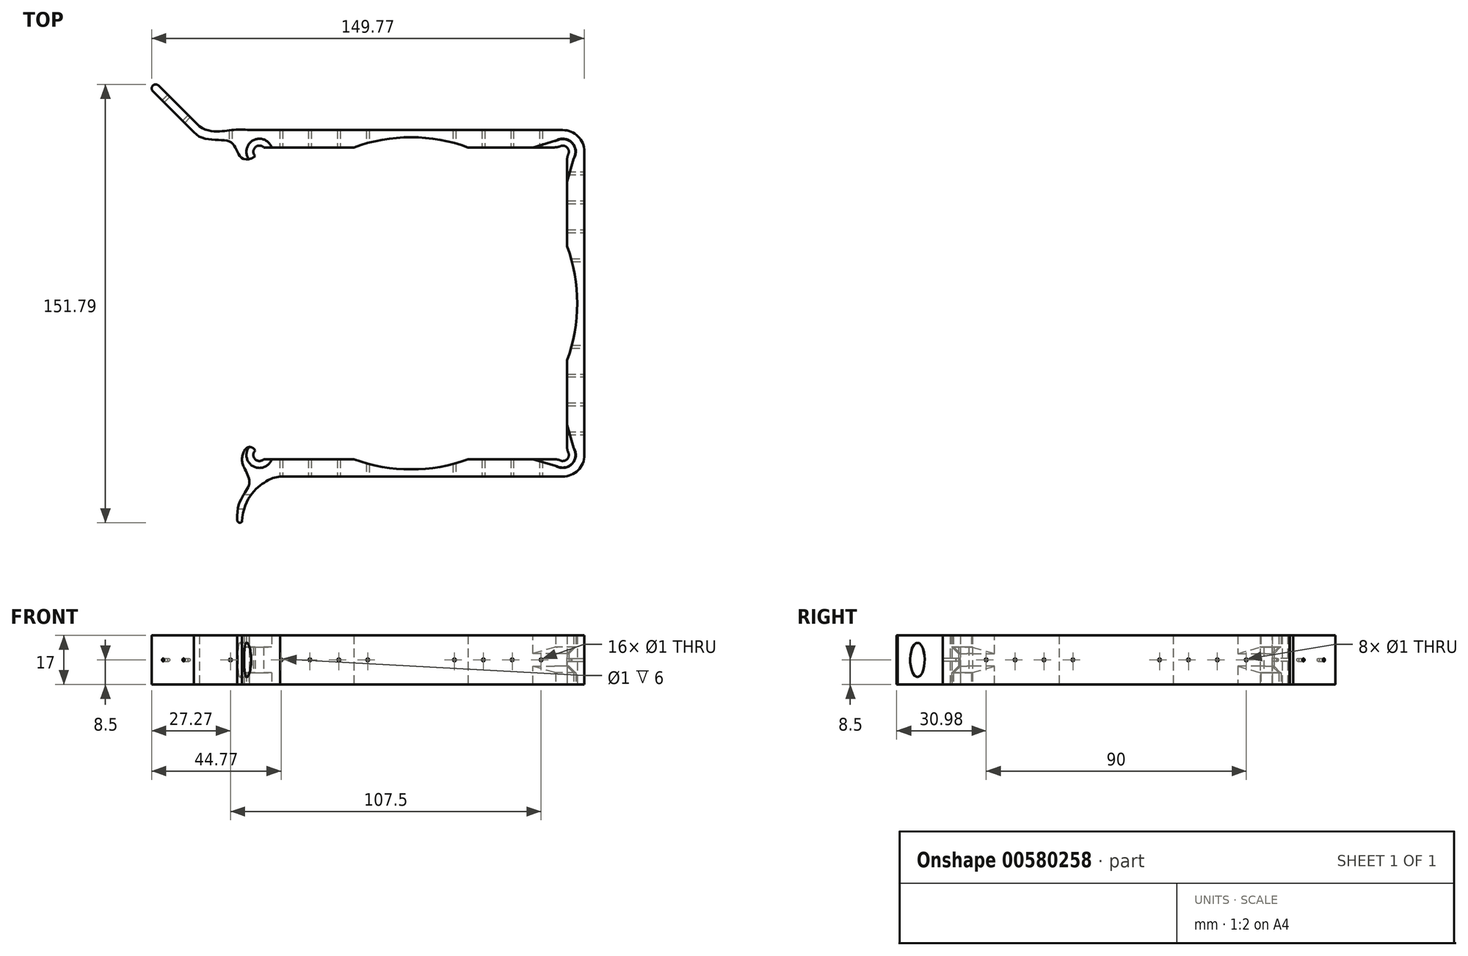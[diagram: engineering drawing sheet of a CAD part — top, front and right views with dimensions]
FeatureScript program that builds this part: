
annotation { "Feature Type Name" : "Feature", "Feature Type Description" : "" }
export const myFeature = defineFeature(function(context is Context, id is Id, definition is map)
    precondition{}
    {
        {
            var Q0;
            Q0=qCreatedBy(makeId("Top.planeOp"),FACE);
            var sketch = newSketch(context, id + "F0", { "sketchPlane" : qUnion([Q0])});
            skLineSegment(sketch, "E0.0", {"start": v(-52.5, 60) * mm, "end": v(52.5, 60) * mm});
            skLineSegment(sketch, "E0.1", {"start": v(60, -52.5) * mm, "end": v(60, 52.5) * mm});
            skArc(sketch, "E0.2", {"start": v(52.5, 60) * mm, "mid": v(57.8, 57.8) * mm, "end": v(60, 52.5) * mm});
            skArc(sketch, "E0.3", {"start": v(60, -52.5) * mm, "mid": v(57.8, -57.8) * mm, "end": v(52.5, -60) * mm});
            skLineSegment(sketch, "E0.4", {"start": v(-52.5, -60) * mm, "end": v(52.5, -60) * mm});
            skCircle(sketch, "E0.6", {"center": v(-52.5, -52.5) * mm, "radius": 2.1 * mm});
            skCircle(sketch, "E0.7", {"center": v(52.5, -52.5) * mm, "radius": 2.1 * mm});
            skCircle(sketch, "E0.8", {"center": v(52.5, 52.5) * mm, "radius": 2.1 * mm});
            skCircle(sketch, "E0.9", {"center": v(-52.5, 52.5) * mm, "radius": 2.1 * mm});
            skLineSegment(sketch, "E1", {"start": v(54, 51.03) * mm, "end": v(54, -51.03) * mm});
            skLineSegment(sketch, "E2", {"start": v(51.03, -54) * mm, "end": v(-51.03, -54) * mm});
            skLineSegment(sketch, "E3", {"start": v(-51.03, 54) * mm, "end": v(51.03, 54) * mm});
            skArc(sketch, "E4", {"start": v(-52.5, -60) * mm, "mid": v(-57.8, -56.8) * mm, "end": v(-57.46, -50.62) * mm});
            skArc(sketch, "E5", {"start": v(-57.46, -50.62) * mm, "mid": v(-55.6, -49.77) * mm, "end": v(-53.98, -51.01) * mm});
            skFitSpline(sketch, "E6", {"points": [v(-52.5, 60) * mm, v(-62.19, 60) * mm, v(-73.29, 61.27) * mm], "startDerivative": vector(-27.31, 0) * mm, "endDerivative": vector(-24.95, 15.44) * mm});
            skFitSpline(sketch, "E7", {"points": [v(-75.23, 59.33) * mm, v(-62.19, 55.68) * mm, v(-57.14, 49.87) * mm], "startDerivative": vector(19.56, -22.5) * mm, "endDerivative": vector(22.3, -1.77) * mm});
            skArc(sketch, "E8", {"start": v(-57.14, 49.87) * mm, "mid": v(-55.44, 50.1) * mm, "end": v(-54, 51.03) * mm});
            skLineSegment(sketch, "E9", {"start": v(-51.03, 54) * mm, "end": v(-54, 51.03) * mm, "construction": true});
            skLineSegment(sketch, "E10", {"start": v(-75.23, 59.33) * mm, "end": v(-73.29, 61.27) * mm, "construction": true});
            skLineSegment(sketch, "E11", {"start": v(-75.23, 59.33) * mm, "end": v(-89.37, 73.47) * mm});
            skLineSegment(sketch, "E12", {"start": v(-73.29, 61.27) * mm, "end": v(-87.43, 75.4) * mm});
            skLineSegment(sketch, "E13", {"start": v(-87.43, 75.4) * mm, "end": v(-89.37, 73.47) * mm});
            skArc(sketch, "E14", {"start": v(-89.37, 73.47) * mm, "mid": v(-89.37, 75.4) * mm, "end": v(-87.43, 75.4) * mm});
            skCircle(sketch, "E15.0", {"center": v(0, 0) * mm, "radius": 57.5 * mm});
            skCircle(sketch, "E16", {"center": v(52.5, 52.5) * mm, "radius": 4.5 * mm});
            skCircle(sketch, "E17", {"center": v(-52.5, 52.5) * mm, "radius": 4.5 * mm});
            skCircle(sketch, "E18", {"center": v(-52.5, -52.5) * mm, "radius": 4.5 * mm});
            skCircle(sketch, "E19", {"center": v(52.5, -52.5) * mm, "radius": 4.5 * mm});
            skFitSpline(sketch, "E20", {"points": [v(-57.8, -56.8) * mm, v(-56.05, -62.69) * mm, v(-60.16, -75.14) * mm], "startDerivative": vector(6.66, -14.28) * mm, "endDerivative": vector(2.44, -37.2) * mm});
            skFitSpline(sketch, "E21", {"points": [v(-45.27, -60) * mm, v(-50.57, -61.9) * mm, v(-58.55, -75.64) * mm], "startDerivative": vector(-16.83, -1.28) * mm, "endDerivative": vector(-1.83, -37.37) * mm});
            skArc(sketch, "E22", {"start": v(-60.16, -75.14) * mm, "mid": v(-59.53, -75.94) * mm, "end": v(-58.55, -75.64) * mm});
            skSolve(sketch);
        }
        {
            var Q0;
            Q0=makeQuery(id+"F0.imprint","IMPRINT",FACE,{"disambiguationData":[TD([[makeQuery(id+"F0.imprint","IMPRINT",EDGE,{"derivedFrom":sQuery(id+"F0.wireOp",EDGE,"E0.0")}),-1.0]])]});
            var Q1;
            Q1=makeQuery(id+"F0.imprint","IMPRINT",FACE,{"disambiguationData":[TD([[makeQuery(id+"F0.imprint","IMPRINT",EDGE,{"derivedFrom":sQuery(id+"F0.wireOp",EDGE,"E13")}),-1.0]])]});
            var Q2;
            {var subQ0=sQuery(id+"F0.wireOp",EDGE,"E3");var subQ1=sQuery(id+"F0.wireOp",EDGE,"E0.9");var subQ2=makeQuery(id+"F0.imprint","INTERSECT",VERTEX,{"derivedFrom":[subQ1,subQ0]});Q2=makeQuery(id+"F0.imprint","IMPRINT",FACE,{"disambiguationData":[TD([[makeQuery(id+"F0.imprint","IMPRINT",EDGE,{"disambiguationData":[TD([[subQ2,-1.0]])],"derivedFrom":subQ1}),-1.0]])]});}
            var Q3;
            {var subQ0=sQuery(id+"F0.wireOp",EDGE,"E1");var subQ1=sQuery(id+"F0.wireOp",EDGE,"E0.8");var subQ2=makeQuery(id+"F0.imprint","INTERSECT",VERTEX,{"derivedFrom":[subQ1,subQ0]});Q3=makeQuery(id+"F0.imprint","IMPRINT",FACE,{"disambiguationData":[TD([[makeQuery(id+"F0.imprint","IMPRINT",EDGE,{"disambiguationData":[TD([[subQ2,-1.0]])],"derivedFrom":subQ1}),-1.0]])]});}
            var Q4;
            {var subQ0=sQuery(id+"F0.wireOp",EDGE,"E1");var subQ1=sQuery(id+"F0.wireOp",EDGE,"E0.7");var subQ2=makeQuery(id+"F0.imprint","INTERSECT",VERTEX,{"derivedFrom":[subQ1,subQ0]});Q4=makeQuery(id+"F0.imprint","IMPRINT",FACE,{"disambiguationData":[TD([[makeQuery(id+"F0.imprint","IMPRINT",EDGE,{"disambiguationData":[TD([[subQ2,1.0]])],"derivedFrom":subQ1}),-1.0]])]});}
            var Q5;
            {var subQ0=sQuery(id+"F0.wireOp",EDGE,"E2");var subQ1=sQuery(id+"F0.wireOp",EDGE,"E0.6");var subQ2=makeQuery(id+"F0.imprint","INTERSECT",VERTEX,{"derivedFrom":[subQ1,subQ0]});Q5=makeQuery(id+"F0.imprint","IMPRINT",FACE,{"disambiguationData":[TD([[makeQuery(id+"F0.imprint","IMPRINT",EDGE,{"disambiguationData":[TD([[subQ2,1.0]])],"derivedFrom":subQ1}),-1.0]])]});}
            extrude(context, id + "F1", {"entities" : qUnion([Q0, Q1, Q2, Q3, Q4, Q5]), "endBound" : BoundingType.SYMMETRIC, "depth" : 9 * mm, "offsetDistance" : 25 * mm});
        }
        {
            var Q0;
            Q0=makeQuery(id+"F0.imprint","IMPRINT",FACE,{"disambiguationData":[TD([[makeQuery(id+"F0.imprint","IMPRINT",EDGE,{"derivedFrom":sQuery(id+"F0.wireOp",EDGE,"E0.0")}),-1.0]])]});
            var Q1;
            Q1=makeQuery(id+"F0.imprint","IMPRINT",FACE,{"disambiguationData":[TD([[makeQuery(id+"F0.imprint","IMPRINT",EDGE,{"derivedFrom":sQuery(id+"F0.wireOp",EDGE,"E13")}),-1.0]])]});
            var Q2;
            {var subQ1=sQuery(id+"F0.wireOp",EDGE,"E20");Q2=makeQuery(id+"F0.imprint","IMPRINT",FACE,{"disambiguationData":[TD([[makeQuery(id+"F0.imprint","IMPRINT",EDGE,{"derivedFrom":subQ1}),1.0]])]});}
            extrude(context, id + "F2", {"entities" : qUnion([Q0, Q1, Q2]), "operationType" : NewBodyOperationType.ADD, "endBound" : BoundingType.SYMMETRIC, "depth" : 17 * mm, "offsetDistance" : 25 * mm});
        }
        {
            var Q0;
            Q0=makeQuery(id+"F1.opExtrude","SWEPT_FACE",FACE,{"disambiguationData":[OSD([sQuery(id+"F0.wireOp",EDGE,"E0.4")])]});
            var sketch = newSketch(context, id + "F3", { "sketchPlane" : qUnion([Q0])});
            skPoint(sketch, "E23", {"position": v(-45, 0) * mm});
            skPoint(sketch, "E23.positionSnap0", {"position": v(-52.5, 0) * mm});
            skPoint(sketch, "E24.1.0.0", {"position": v(-35, 0) * mm});
            skPoint(sketch, "E24.2.0.0", {"position": v(-25, 0) * mm});
            skPoint(sketch, "E24.3.0.0", {"position": v(-15, 0) * mm});
            skPoint(sketch, "E24.4.0.0", {"position": v(-5, 0) * mm});
            skPoint(sketch, "E24.5.0.0", {"position": v(5, 0) * mm});
            skPoint(sketch, "E24.6.0.0", {"position": v(15, 0) * mm});
            skPoint(sketch, "E24.7.0.0", {"position": v(25, 0) * mm});
            skPoint(sketch, "E24.8.0.0", {"position": v(35, 0) * mm});
            skPoint(sketch, "E24.9.0.0", {"position": v(45, 0) * mm});
            skLineSegment(sketch, "E24.direction1", {"start": v(-45, 0) * mm, "end": v(-35, 0) * mm, "construction": true});
            skPoint(sketch, "E25", {"position": v(-62.5, 0) * mm});
            skSolve(sketch);
        }
        {
            var Q0;
            Q0=sQuery(id+"F3.wireOp",VERTEX,"E23");
            var Q1;
            Q1=sQuery(id+"F3.wireOp",VERTEX,"E24.1.0.0");
            var Q2;
            Q2=sQuery(id+"F3.wireOp",VERTEX,"E24.2.0.0");
            var Q3;
            Q3=sQuery(id+"F3.wireOp",VERTEX,"E24.3.0.0");
            var Q4;
            Q4=sQuery(id+"F3.wireOp",VERTEX,"E24.6.0.0");
            var Q5;
            Q5=sQuery(id+"F3.wireOp",VERTEX,"E24.7.0.0");
            var Q6;
            Q6=sQuery(id+"F3.wireOp",VERTEX,"E24.8.0.0");
            var Q7;
            Q7=sQuery(id+"F3.wireOp",VERTEX,"E24.9.0.0");
            var Q8;
            Q8=sQuery(id+"F3.wireOp",VERTEX,"E25");
            var Q9;
            Q9=makeQuery(id+"F1.opExtrude","SWEPT_BODY",BODY,{"disambiguationData":[OSD([sQuery(id+"F0.wireOp",EDGE,"E0.0"),sQuery(id+"F0.wireOp",EDGE,"E0.1"),sQuery(id+"F0.wireOp",EDGE,"E0.2"),sQuery(id+"F0.wireOp",EDGE,"E0.3"),sQuery(id+"F0.wireOp",EDGE,"E0.4"),sQuery(id+"F0.wireOp",EDGE,"E0.6"),sQuery(id+"F0.wireOp",EDGE,"E0.7"),sQuery(id+"F0.wireOp",EDGE,"E0.8"),sQuery(id+"F0.wireOp",EDGE,"E0.9"),sQuery(id+"F0.wireOp",EDGE,"E1"),sQuery(id+"F0.wireOp",EDGE,"E2"),sQuery(id+"F0.wireOp",EDGE,"E3"),sQuery(id+"F0.wireOp",EDGE,"E4"),sQuery(id+"F0.wireOp",EDGE,"E5"),sQuery(id+"F0.wireOp",EDGE,"E6"),sQuery(id+"F0.wireOp",EDGE,"E7"),sQuery(id+"F0.wireOp",EDGE,"E8"),sQuery(id+"F0.wireOp",EDGE,"E11"),sQuery(id+"F0.wireOp",EDGE,"E12"),sQuery(id+"F0.wireOp",EDGE,"E14"),sQuery(id+"F0.wireOp",EDGE,"E15.0")])]});
            hole(context, id + "F4", {"style" : HoleStyle.SIMPLE, "endStyle" : HoleEndStyle.THROUGH, "holeDiameter" : 1 * mm, "isTappedThrough" : true, "tappedDepth" : 12 * mm, "tapClearance" : 3, "locations" : qUnion([Q0, Q1, Q2, Q3, Q4, Q5, Q6, Q7, Q8]), "scope" : qUnion([Q9])});
        }
        {
            var Q0;
            Q0=makeQuery(id+"F1.opExtrude","SWEPT_FACE",FACE,{"disambiguationData":[OSD([sQuery(id+"F0.wireOp",EDGE,"E0.1")])]});
            var sketch = newSketch(context, id + "F5", { "sketchPlane" : qUnion([Q0])});
            skPoint(sketch, "E26", {"position": v(-45, 0) * mm});
            skPoint(sketch, "E26.positionSnap0", {"position": v(-52.5, 0) * mm});
            skPoint(sketch, "E27.1.0.0", {"position": v(-35, 0) * mm});
            skPoint(sketch, "E27.2.0.0", {"position": v(-25, 0) * mm});
            skPoint(sketch, "E27.3.0.0", {"position": v(-15, 0) * mm});
            skPoint(sketch, "E27.4.0.0", {"position": v(-5, 0) * mm});
            skPoint(sketch, "E27.5.0.0", {"position": v(5, 0) * mm});
            skPoint(sketch, "E27.6.0.0", {"position": v(15, 0) * mm});
            skPoint(sketch, "E27.7.0.0", {"position": v(25, 0) * mm});
            skPoint(sketch, "E27.8.0.0", {"position": v(35, 0) * mm});
            skPoint(sketch, "E27.9.0.0", {"position": v(45, 0) * mm});
            skLineSegment(sketch, "E27.direction1", {"start": v(-47.5, 4.5) * mm, "end": v(-37.5, 4.5) * mm, "construction": true});
            skSolve(sketch);
        }
        {
            var Q0;
            Q0=sQuery(id+"F5.wireOp",VERTEX,"E26");
            var Q1;
            Q1=sQuery(id+"F5.wireOp",VERTEX,"E27.1.0.0");
            var Q2;
            Q2=sQuery(id+"F5.wireOp",VERTEX,"E27.2.0.0");
            var Q3;
            Q3=sQuery(id+"F5.wireOp",VERTEX,"E27.6.0.0");
            var Q4;
            Q4=sQuery(id+"F5.wireOp",VERTEX,"E27.7.0.0");
            var Q5;
            Q5=sQuery(id+"F5.wireOp",VERTEX,"E27.8.0.0");
            var Q6;
            Q6=sQuery(id+"F5.wireOp",VERTEX,"E27.9.0.0");
            var Q7;
            Q7=sQuery(id+"F5.wireOp",VERTEX,"E27.3.0.0");
            var Q8;
            Q8=makeQuery(id+"F1.opExtrude","SWEPT_BODY",BODY,{"disambiguationData":[OSD([sQuery(id+"F0.wireOp",EDGE,"E0.0"),sQuery(id+"F0.wireOp",EDGE,"E0.1"),sQuery(id+"F0.wireOp",EDGE,"E0.2"),sQuery(id+"F0.wireOp",EDGE,"E0.3"),sQuery(id+"F0.wireOp",EDGE,"E0.4"),sQuery(id+"F0.wireOp",EDGE,"E0.6"),sQuery(id+"F0.wireOp",EDGE,"E0.7"),sQuery(id+"F0.wireOp",EDGE,"E0.8"),sQuery(id+"F0.wireOp",EDGE,"E0.9"),sQuery(id+"F0.wireOp",EDGE,"E1"),sQuery(id+"F0.wireOp",EDGE,"E2"),sQuery(id+"F0.wireOp",EDGE,"E3"),sQuery(id+"F0.wireOp",EDGE,"E4"),sQuery(id+"F0.wireOp",EDGE,"E5"),sQuery(id+"F0.wireOp",EDGE,"E6"),sQuery(id+"F0.wireOp",EDGE,"E7"),sQuery(id+"F0.wireOp",EDGE,"E8"),sQuery(id+"F0.wireOp",EDGE,"E11"),sQuery(id+"F0.wireOp",EDGE,"E12"),sQuery(id+"F0.wireOp",EDGE,"E14"),sQuery(id+"F0.wireOp",EDGE,"E15.0")])]});
            hole(context, id + "F6", {"style" : HoleStyle.SIMPLE, "endStyle" : HoleEndStyle.THROUGH, "holeDiameter" : 1 * mm, "isTappedThrough" : true, "tappedDepth" : 12 * mm, "tapClearance" : 3, "locations" : qUnion([Q0, Q1, Q2, Q3, Q4, Q5, Q6, Q7]), "scope" : qUnion([Q8])});
        }
        {
            var Q0;
            Q0=makeQuery(id+"F1.opExtrude","SWEPT_FACE",FACE,{"disambiguationData":[OSD([sQuery(id+"F0.wireOp",EDGE,"E12")])]});
            var sketch = newSketch(context, id + "F7", { "sketchPlane" : qUnion([Q0])});
            skPoint(sketch, "E28", {"position": v(110.15, 0) * mm});
            skPoint(sketch, "E28.positionSnap0", {"position": v(115.15, 0) * mm});
            skPoint(sketch, "E29.1.0.0", {"position": v(100.15, 0) * mm});
            skPoint(sketch, "E29.2.0.0", {"position": v(90.15, 0) * mm});
            skLineSegment(sketch, "E29.direction1", {"start": v(110.15, 0) * mm, "end": v(100.15, 0) * mm, "construction": true});
            skSolve(sketch);
        }
        {
            var Q0;
            Q0=sQuery(id+"F7.wireOp",VERTEX,"E28");
            var Q1;
            Q1=sQuery(id+"F7.wireOp",VERTEX,"E29.1.0.0");
            var Q2;
            Q2=makeQuery(id+"F1.opExtrude","SWEPT_BODY",BODY,{"disambiguationData":[OSD([sQuery(id+"F0.wireOp",EDGE,"E0.0"),sQuery(id+"F0.wireOp",EDGE,"E0.1"),sQuery(id+"F0.wireOp",EDGE,"E0.2"),sQuery(id+"F0.wireOp",EDGE,"E0.3"),sQuery(id+"F0.wireOp",EDGE,"E0.4"),sQuery(id+"F0.wireOp",EDGE,"E0.6"),sQuery(id+"F0.wireOp",EDGE,"E0.7"),sQuery(id+"F0.wireOp",EDGE,"E0.8"),sQuery(id+"F0.wireOp",EDGE,"E0.9"),sQuery(id+"F0.wireOp",EDGE,"E1"),sQuery(id+"F0.wireOp",EDGE,"E2"),sQuery(id+"F0.wireOp",EDGE,"E3"),sQuery(id+"F0.wireOp",EDGE,"E4"),sQuery(id+"F0.wireOp",EDGE,"E5"),sQuery(id+"F0.wireOp",EDGE,"E6"),sQuery(id+"F0.wireOp",EDGE,"E7"),sQuery(id+"F0.wireOp",EDGE,"E8"),sQuery(id+"F0.wireOp",EDGE,"E11"),sQuery(id+"F0.wireOp",EDGE,"E12"),sQuery(id+"F0.wireOp",EDGE,"E14"),sQuery(id+"F0.wireOp",EDGE,"E15.0")])]});
            hole(context, id + "F8", {"style" : HoleStyle.SIMPLE, "endStyle" : HoleEndStyle.THROUGH, "holeDiameter" : 1 * mm, "isTappedThrough" : true, "tappedDepth" : 12 * mm, "tapClearance" : 3, "locations" : qUnion([Q0, Q1]), "scope" : qUnion([Q2])});
        }
        {
            var Q0;
            Q0=qCreatedBy(makeId("Right.planeOp"),FACE);
            var sketch = newSketch(context, id + "F9", { "sketchPlane" : qUnion([Q0])});
            skEllipse(sketch, "E30", {"center": v(-68.8, 0) * mm, "majorRadius": 6 * mm, "minorRadius": 2.5 * mm, "majorAxis": v(0, -1)});
            skSolve(sketch);
        }
        {
            var Q0;
            Q0=makeQuery(id+"F9.imprint","IMPRINT",FACE,{"disambiguationData":[TD([[makeQuery(id+"F9.imprint","IMPRINT",EDGE,{"derivedFrom":sQuery(id+"F9.wireOp",EDGE,"E30")}),1.0]])]});
            var Q1;
            Q1=sQuery(id+"F9.wireOp",EDGE,"E30");
            extrude(context, id + "F10", {"entities" : qUnion([Q0]), "operationType" : NewBodyOperationType.REMOVE, "surfaceEntities" : qUnion([Q1]), "oppositeDirection" : true, "depth" : 80 * mm, "offsetDistance" : 25 * mm});
        }
        {
            var Q0;
            Q0=makeQuery(id+"F1.opExtrude","SWEPT_EDGE",EDGE,{"disambiguationData":[OSD([sQuery(id+"F0.wireOp",EDGE,"E0.8"),sQuery(id+"F0.wireOp",EDGE,"E1")])]});
            var Q1;
            Q1=makeQuery(id+"F1.opExtrude","SWEPT_EDGE",EDGE,{"disambiguationData":[OSD([sQuery(id+"F0.wireOp",EDGE,"E0.8"),sQuery(id+"F0.wireOp",EDGE,"E3")])]});
            var Q2;
            Q2=makeQuery(id+"F1.opExtrude","SWEPT_EDGE",EDGE,{"disambiguationData":[OSD([sQuery(id+"F0.wireOp",EDGE,"E0.7"),sQuery(id+"F0.wireOp",EDGE,"E2")])]});
            var Q3;
            Q3=makeQuery(id+"F1.opExtrude","SWEPT_EDGE",EDGE,{"disambiguationData":[OSD([sQuery(id+"F0.wireOp",EDGE,"E0.7"),sQuery(id+"F0.wireOp",EDGE,"E1")])]});
            fillet(context, id + "F11", {"entities" : qUnion([Q0, Q1, Q2, Q3]), "radius" : 5 * mm, "tangentPropagation" : true, "allowEdgeOverflow" : false});
        }
        {
            var Q0;
            {var subQ0=sQuery(id+"F0.wireOp",EDGE,"E15.0");var subQ1=sQuery(id+"F0.wireOp",EDGE,"E3");var subQ2=sQuery(id+"F0.wireOp",EDGE,"E16");var subQ5=sQuery(id+"F0.wireOp",EDGE,"E0.8");var subQ6=sQuery(id+"F0.wireOp",EDGE,"E14");var subQ7=sQuery(id+"F0.wireOp",EDGE,"E12");var subQ8=sQuery(id+"F0.wireOp",EDGE,"E11");var subQ9=sQuery(id+"F0.wireOp",EDGE,"E8");var subQ10=sQuery(id+"F0.wireOp",EDGE,"E7");var subQ11=sQuery(id+"F0.wireOp",EDGE,"E6");var subQ12=sQuery(id+"F0.wireOp",EDGE,"E5");var subQ13=sQuery(id+"F0.wireOp",EDGE,"E4");var subQ14=sQuery(id+"F0.wireOp",EDGE,"E2");var subQ15=sQuery(id+"F0.wireOp",EDGE,"E1");var subQ16=sQuery(id+"F0.wireOp",EDGE,"E0.4");var subQ17=sQuery(id+"F0.wireOp",EDGE,"E0.3");var subQ18=sQuery(id+"F0.wireOp",EDGE,"E0.2");var subQ19=sQuery(id+"F0.wireOp",EDGE,"E0.1");var subQ20=sQuery(id+"F0.wireOp",EDGE,"E0.0");Q0=makeQuery(id+"F2.boolean.opBoolean","SPLIT",EDGE,{"disambiguationData":[TD([makeQuery(id+"F1.opExtrude","CAP_FACE",FACE,{"disambiguationData":[OSD([subQ20,subQ19,subQ18,subQ17,subQ16,sQuery(id+"F0.wireOp",EDGE,"E0.6"),sQuery(id+"F0.wireOp",EDGE,"E0.7"),subQ5,sQuery(id+"F0.wireOp",EDGE,"E0.9"),subQ15,subQ14,subQ1,subQ13,subQ12,subQ11,subQ10,subQ9,subQ8,subQ7,subQ6,subQ0])],"isStart":false})])],"derivedFrom":makeQuery(id+"F2.opExtrude","SWEPT_EDGE",EDGE,{"disambiguationData":[OSD([subQ1,subQ2])]})});}
            var Q1;
            {var subQ0=sQuery(id+"F0.wireOp",EDGE,"E16");var subQ1=sQuery(id+"F0.wireOp",EDGE,"E1");var subQ3=sQuery(id+"F0.wireOp",EDGE,"E15.0");var subQ5=sQuery(id+"F0.wireOp",EDGE,"E0.8");var subQ6=sQuery(id+"F0.wireOp",EDGE,"E14");var subQ7=sQuery(id+"F0.wireOp",EDGE,"E12");var subQ8=sQuery(id+"F0.wireOp",EDGE,"E11");var subQ9=sQuery(id+"F0.wireOp",EDGE,"E8");var subQ10=sQuery(id+"F0.wireOp",EDGE,"E7");var subQ11=sQuery(id+"F0.wireOp",EDGE,"E6");var subQ12=sQuery(id+"F0.wireOp",EDGE,"E5");var subQ13=sQuery(id+"F0.wireOp",EDGE,"E4");var subQ14=sQuery(id+"F0.wireOp",EDGE,"E3");var subQ15=sQuery(id+"F0.wireOp",EDGE,"E2");var subQ16=sQuery(id+"F0.wireOp",EDGE,"E0.4");var subQ17=sQuery(id+"F0.wireOp",EDGE,"E0.3");var subQ18=sQuery(id+"F0.wireOp",EDGE,"E0.2");var subQ19=sQuery(id+"F0.wireOp",EDGE,"E0.1");var subQ20=sQuery(id+"F0.wireOp",EDGE,"E0.0");Q1=makeQuery(id+"F2.boolean.opBoolean","SPLIT",EDGE,{"disambiguationData":[TD([makeQuery(id+"F1.opExtrude","CAP_FACE",FACE,{"disambiguationData":[OSD([subQ20,subQ19,subQ18,subQ17,subQ16,sQuery(id+"F0.wireOp",EDGE,"E0.6"),sQuery(id+"F0.wireOp",EDGE,"E0.7"),subQ5,sQuery(id+"F0.wireOp",EDGE,"E0.9"),subQ1,subQ15,subQ14,subQ13,subQ12,subQ11,subQ10,subQ9,subQ8,subQ7,subQ6,subQ3])],"isStart":false})])],"derivedFrom":makeQuery(id+"F2.opExtrude","SWEPT_EDGE",EDGE,{"disambiguationData":[OSD([subQ1,subQ0])]})});}
            var Q2;
            {var subQ0=sQuery(id+"F0.wireOp",EDGE,"E16");var subQ1=sQuery(id+"F0.wireOp",EDGE,"E1");var subQ3=sQuery(id+"F0.wireOp",EDGE,"E15.0");var subQ5=sQuery(id+"F0.wireOp",EDGE,"E0.8");var subQ6=sQuery(id+"F0.wireOp",EDGE,"E14");var subQ7=sQuery(id+"F0.wireOp",EDGE,"E12");var subQ8=sQuery(id+"F0.wireOp",EDGE,"E11");var subQ9=sQuery(id+"F0.wireOp",EDGE,"E8");var subQ10=sQuery(id+"F0.wireOp",EDGE,"E7");var subQ11=sQuery(id+"F0.wireOp",EDGE,"E6");var subQ12=sQuery(id+"F0.wireOp",EDGE,"E5");var subQ13=sQuery(id+"F0.wireOp",EDGE,"E4");var subQ14=sQuery(id+"F0.wireOp",EDGE,"E3");var subQ15=sQuery(id+"F0.wireOp",EDGE,"E2");var subQ16=sQuery(id+"F0.wireOp",EDGE,"E0.4");var subQ17=sQuery(id+"F0.wireOp",EDGE,"E0.3");var subQ18=sQuery(id+"F0.wireOp",EDGE,"E0.2");var subQ19=sQuery(id+"F0.wireOp",EDGE,"E0.1");var subQ20=sQuery(id+"F0.wireOp",EDGE,"E0.0");Q2=makeQuery(id+"F2.boolean.opBoolean","SPLIT",EDGE,{"disambiguationData":[TD([makeQuery(id+"F1.opExtrude","CAP_FACE",FACE,{"disambiguationData":[OSD([subQ20,subQ19,subQ18,subQ17,subQ16,sQuery(id+"F0.wireOp",EDGE,"E0.6"),sQuery(id+"F0.wireOp",EDGE,"E0.7"),subQ5,sQuery(id+"F0.wireOp",EDGE,"E0.9"),subQ1,subQ15,subQ14,subQ13,subQ12,subQ11,subQ10,subQ9,subQ8,subQ7,subQ6,subQ3])],"isStart":true})])],"derivedFrom":makeQuery(id+"F2.opExtrude","SWEPT_EDGE",EDGE,{"disambiguationData":[OSD([subQ1,subQ0])]})});}
            var Q3;
            {var subQ0=sQuery(id+"F0.wireOp",EDGE,"E15.0");var subQ1=sQuery(id+"F0.wireOp",EDGE,"E3");var subQ2=sQuery(id+"F0.wireOp",EDGE,"E16");var subQ5=sQuery(id+"F0.wireOp",EDGE,"E14");var subQ6=sQuery(id+"F0.wireOp",EDGE,"E12");var subQ7=sQuery(id+"F0.wireOp",EDGE,"E11");var subQ8=sQuery(id+"F0.wireOp",EDGE,"E8");var subQ9=sQuery(id+"F0.wireOp",EDGE,"E7");var subQ10=sQuery(id+"F0.wireOp",EDGE,"E6");var subQ11=sQuery(id+"F0.wireOp",EDGE,"E5");var subQ12=sQuery(id+"F0.wireOp",EDGE,"E4");var subQ13=sQuery(id+"F0.wireOp",EDGE,"E2");var subQ14=sQuery(id+"F0.wireOp",EDGE,"E1");var subQ15=sQuery(id+"F0.wireOp",EDGE,"E0.4");var subQ16=sQuery(id+"F0.wireOp",EDGE,"E0.3");var subQ17=sQuery(id+"F0.wireOp",EDGE,"E0.2");var subQ18=sQuery(id+"F0.wireOp",EDGE,"E0.1");var subQ19=sQuery(id+"F0.wireOp",EDGE,"E0.0");var subQ20=sQuery(id+"F0.wireOp",EDGE,"E0.8");Q3=makeQuery(id+"F2.boolean.opBoolean","SPLIT",EDGE,{"disambiguationData":[TD([makeQuery(id+"F1.opExtrude","CAP_FACE",FACE,{"disambiguationData":[OSD([subQ19,subQ18,subQ17,subQ16,subQ15,sQuery(id+"F0.wireOp",EDGE,"E0.6"),sQuery(id+"F0.wireOp",EDGE,"E0.7"),subQ20,sQuery(id+"F0.wireOp",EDGE,"E0.9"),subQ14,subQ13,subQ1,subQ12,subQ11,subQ10,subQ9,subQ8,subQ7,subQ6,subQ5,subQ0])],"isStart":true})])],"derivedFrom":makeQuery(id+"F2.opExtrude","SWEPT_EDGE",EDGE,{"disambiguationData":[OSD([subQ1,subQ2])]})});}
            var Q4;
            {var subQ0=sQuery(id+"F0.wireOp",EDGE,"E15.0");var subQ1=sQuery(id+"F0.wireOp",EDGE,"E1");var subQ2=sQuery(id+"F0.wireOp",EDGE,"E19");var subQ5=sQuery(id+"F0.wireOp",EDGE,"E0.7");var subQ6=sQuery(id+"F0.wireOp",EDGE,"E14");var subQ7=sQuery(id+"F0.wireOp",EDGE,"E12");var subQ8=sQuery(id+"F0.wireOp",EDGE,"E11");var subQ9=sQuery(id+"F0.wireOp",EDGE,"E8");var subQ10=sQuery(id+"F0.wireOp",EDGE,"E7");var subQ11=sQuery(id+"F0.wireOp",EDGE,"E6");var subQ12=sQuery(id+"F0.wireOp",EDGE,"E5");var subQ13=sQuery(id+"F0.wireOp",EDGE,"E4");var subQ14=sQuery(id+"F0.wireOp",EDGE,"E3");var subQ15=sQuery(id+"F0.wireOp",EDGE,"E2");var subQ16=sQuery(id+"F0.wireOp",EDGE,"E0.4");var subQ17=sQuery(id+"F0.wireOp",EDGE,"E0.3");var subQ18=sQuery(id+"F0.wireOp",EDGE,"E0.2");var subQ19=sQuery(id+"F0.wireOp",EDGE,"E0.1");var subQ20=sQuery(id+"F0.wireOp",EDGE,"E0.0");Q4=makeQuery(id+"F2.boolean.opBoolean","SPLIT",EDGE,{"disambiguationData":[TD([makeQuery(id+"F1.opExtrude","CAP_FACE",FACE,{"disambiguationData":[OSD([subQ20,subQ19,subQ18,subQ17,subQ16,sQuery(id+"F0.wireOp",EDGE,"E0.6"),subQ5,sQuery(id+"F0.wireOp",EDGE,"E0.8"),sQuery(id+"F0.wireOp",EDGE,"E0.9"),subQ1,subQ15,subQ14,subQ13,subQ12,subQ11,subQ10,subQ9,subQ8,subQ7,subQ6,subQ0])],"isStart":false})])],"derivedFrom":makeQuery(id+"F2.opExtrude","SWEPT_EDGE",EDGE,{"disambiguationData":[OSD([subQ1,subQ2])]})});}
            var Q5;
            {var subQ0=sQuery(id+"F0.wireOp",EDGE,"E19");var subQ1=sQuery(id+"F0.wireOp",EDGE,"E2");var subQ3=sQuery(id+"F0.wireOp",EDGE,"E15.0");var subQ5=sQuery(id+"F0.wireOp",EDGE,"E0.7");var subQ6=sQuery(id+"F0.wireOp",EDGE,"E14");var subQ7=sQuery(id+"F0.wireOp",EDGE,"E12");var subQ8=sQuery(id+"F0.wireOp",EDGE,"E11");var subQ9=sQuery(id+"F0.wireOp",EDGE,"E8");var subQ10=sQuery(id+"F0.wireOp",EDGE,"E7");var subQ11=sQuery(id+"F0.wireOp",EDGE,"E6");var subQ12=sQuery(id+"F0.wireOp",EDGE,"E5");var subQ13=sQuery(id+"F0.wireOp",EDGE,"E4");var subQ14=sQuery(id+"F0.wireOp",EDGE,"E3");var subQ15=sQuery(id+"F0.wireOp",EDGE,"E1");var subQ16=sQuery(id+"F0.wireOp",EDGE,"E0.4");var subQ17=sQuery(id+"F0.wireOp",EDGE,"E0.3");var subQ18=sQuery(id+"F0.wireOp",EDGE,"E0.2");var subQ19=sQuery(id+"F0.wireOp",EDGE,"E0.1");var subQ20=sQuery(id+"F0.wireOp",EDGE,"E0.0");Q5=makeQuery(id+"F2.boolean.opBoolean","SPLIT",EDGE,{"disambiguationData":[TD([makeQuery(id+"F1.opExtrude","CAP_FACE",FACE,{"disambiguationData":[OSD([subQ20,subQ19,subQ18,subQ17,subQ16,sQuery(id+"F0.wireOp",EDGE,"E0.6"),subQ5,sQuery(id+"F0.wireOp",EDGE,"E0.8"),sQuery(id+"F0.wireOp",EDGE,"E0.9"),subQ15,subQ1,subQ14,subQ13,subQ12,subQ11,subQ10,subQ9,subQ8,subQ7,subQ6,subQ3])],"isStart":false})])],"derivedFrom":makeQuery(id+"F2.opExtrude","SWEPT_EDGE",EDGE,{"disambiguationData":[OSD([subQ1,subQ0])]})});}
            var Q6;
            {var subQ0=sQuery(id+"F0.wireOp",EDGE,"E19");var subQ1=sQuery(id+"F0.wireOp",EDGE,"E2");var subQ3=sQuery(id+"F0.wireOp",EDGE,"E15.0");var subQ5=sQuery(id+"F0.wireOp",EDGE,"E0.7");var subQ6=sQuery(id+"F0.wireOp",EDGE,"E14");var subQ7=sQuery(id+"F0.wireOp",EDGE,"E12");var subQ8=sQuery(id+"F0.wireOp",EDGE,"E11");var subQ9=sQuery(id+"F0.wireOp",EDGE,"E8");var subQ10=sQuery(id+"F0.wireOp",EDGE,"E7");var subQ11=sQuery(id+"F0.wireOp",EDGE,"E6");var subQ12=sQuery(id+"F0.wireOp",EDGE,"E5");var subQ13=sQuery(id+"F0.wireOp",EDGE,"E4");var subQ14=sQuery(id+"F0.wireOp",EDGE,"E3");var subQ15=sQuery(id+"F0.wireOp",EDGE,"E1");var subQ16=sQuery(id+"F0.wireOp",EDGE,"E0.4");var subQ17=sQuery(id+"F0.wireOp",EDGE,"E0.3");var subQ18=sQuery(id+"F0.wireOp",EDGE,"E0.2");var subQ19=sQuery(id+"F0.wireOp",EDGE,"E0.1");var subQ20=sQuery(id+"F0.wireOp",EDGE,"E0.0");Q6=makeQuery(id+"F2.boolean.opBoolean","SPLIT",EDGE,{"disambiguationData":[TD([makeQuery(id+"F1.opExtrude","CAP_FACE",FACE,{"disambiguationData":[OSD([subQ20,subQ19,subQ18,subQ17,subQ16,sQuery(id+"F0.wireOp",EDGE,"E0.6"),subQ5,sQuery(id+"F0.wireOp",EDGE,"E0.8"),sQuery(id+"F0.wireOp",EDGE,"E0.9"),subQ15,subQ1,subQ14,subQ13,subQ12,subQ11,subQ10,subQ9,subQ8,subQ7,subQ6,subQ3])],"isStart":true})])],"derivedFrom":makeQuery(id+"F2.opExtrude","SWEPT_EDGE",EDGE,{"disambiguationData":[OSD([subQ1,subQ0])]})});}
            var Q7;
            {var subQ0=sQuery(id+"F0.wireOp",EDGE,"E15.0");var subQ1=sQuery(id+"F0.wireOp",EDGE,"E1");var subQ2=sQuery(id+"F0.wireOp",EDGE,"E19");var subQ5=sQuery(id+"F0.wireOp",EDGE,"E0.7");var subQ6=sQuery(id+"F0.wireOp",EDGE,"E14");var subQ7=sQuery(id+"F0.wireOp",EDGE,"E12");var subQ8=sQuery(id+"F0.wireOp",EDGE,"E11");var subQ9=sQuery(id+"F0.wireOp",EDGE,"E8");var subQ10=sQuery(id+"F0.wireOp",EDGE,"E7");var subQ11=sQuery(id+"F0.wireOp",EDGE,"E6");var subQ12=sQuery(id+"F0.wireOp",EDGE,"E5");var subQ13=sQuery(id+"F0.wireOp",EDGE,"E4");var subQ14=sQuery(id+"F0.wireOp",EDGE,"E3");var subQ15=sQuery(id+"F0.wireOp",EDGE,"E2");var subQ16=sQuery(id+"F0.wireOp",EDGE,"E0.4");var subQ17=sQuery(id+"F0.wireOp",EDGE,"E0.3");var subQ18=sQuery(id+"F0.wireOp",EDGE,"E0.2");var subQ19=sQuery(id+"F0.wireOp",EDGE,"E0.1");var subQ20=sQuery(id+"F0.wireOp",EDGE,"E0.0");Q7=makeQuery(id+"F2.boolean.opBoolean","SPLIT",EDGE,{"disambiguationData":[TD([makeQuery(id+"F1.opExtrude","CAP_FACE",FACE,{"disambiguationData":[OSD([subQ20,subQ19,subQ18,subQ17,subQ16,sQuery(id+"F0.wireOp",EDGE,"E0.6"),subQ5,sQuery(id+"F0.wireOp",EDGE,"E0.8"),sQuery(id+"F0.wireOp",EDGE,"E0.9"),subQ1,subQ15,subQ14,subQ13,subQ12,subQ11,subQ10,subQ9,subQ8,subQ7,subQ6,subQ0])],"isStart":true})])],"derivedFrom":makeQuery(id+"F2.opExtrude","SWEPT_EDGE",EDGE,{"disambiguationData":[OSD([subQ1,subQ2])]})});}
            chamfer(context, id + "F12", {"entities" : qUnion([Q0, Q1, Q2, Q3, Q4, Q5, Q6, Q7]), "width" : 15 * mm, "tangentPropagation" : true});
        }
        {
            var Q0;
            Q0=makeQuery(id+"F1.opExtrude","CAP_EDGE",EDGE,{"disambiguationData":[OSD([sQuery(id+"F0.wireOp",EDGE,"E0.8")])],"isStart":false});
            var Q1;
            Q1=makeQuery(id+"F1.opExtrude","CAP_EDGE",EDGE,{"disambiguationData":[OSD([sQuery(id+"F0.wireOp",EDGE,"E0.8")])],"isStart":true});
            var Q2;
            Q2=makeQuery(id+"F1.opExtrude","CAP_EDGE",EDGE,{"disambiguationData":[OSD([sQuery(id+"F0.wireOp",EDGE,"E0.7")])],"isStart":false});
            var Q3;
            Q3=makeQuery(id+"F1.opExtrude","CAP_EDGE",EDGE,{"disambiguationData":[OSD([sQuery(id+"F0.wireOp",EDGE,"E0.7")])],"isStart":true});
            chamfer(context, id + "F13", {"entities" : qUnion([Q0, Q1, Q2, Q3]), "width" : 2.3 * mm, "tangentPropagation" : true});
        }
    });
